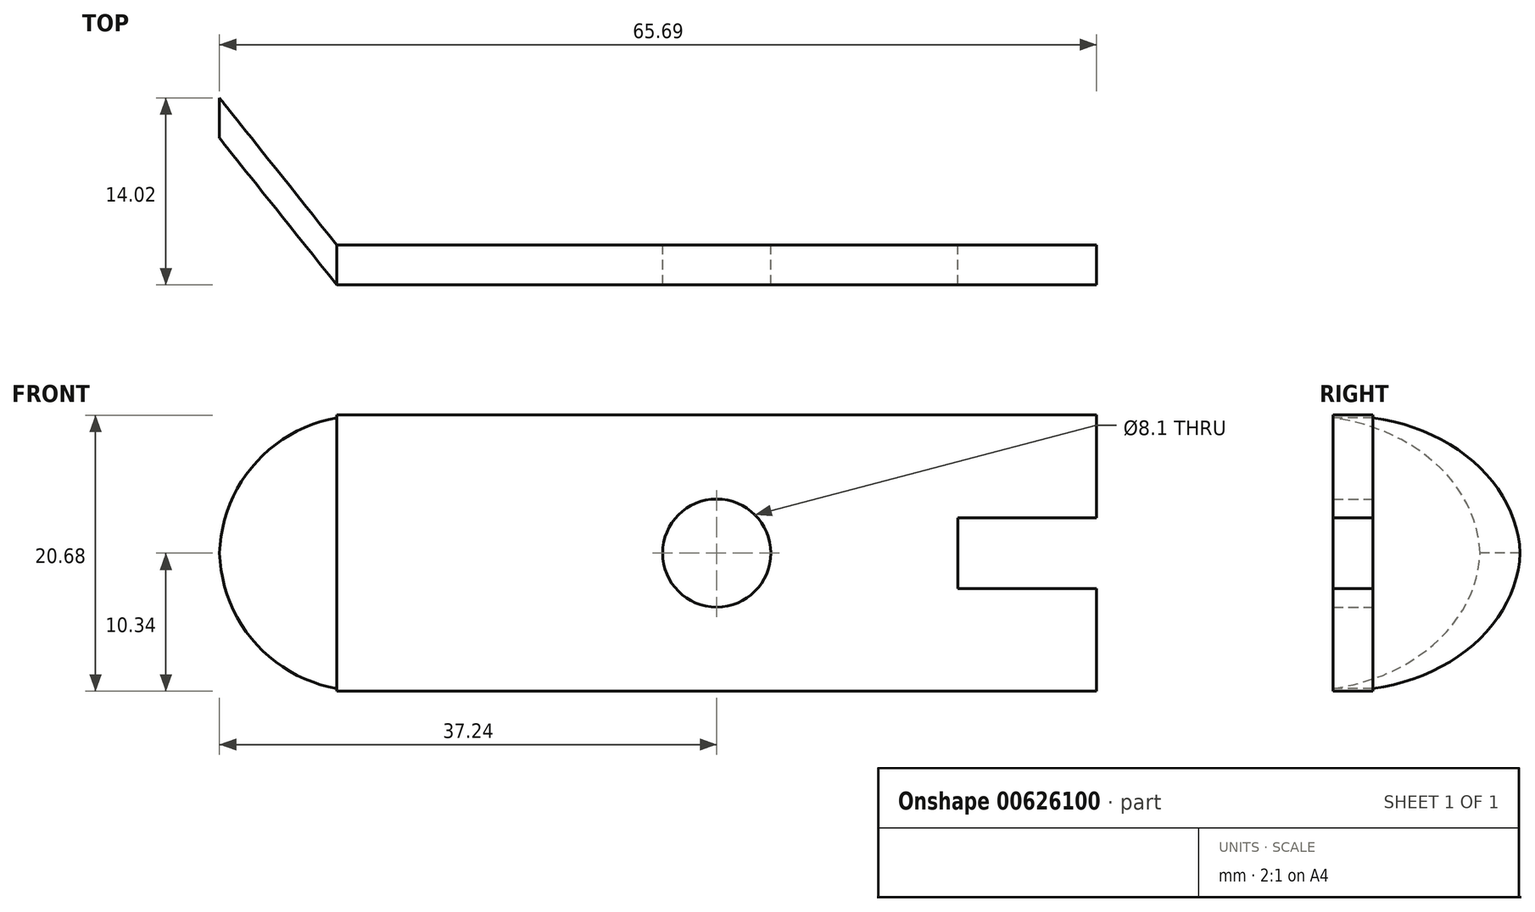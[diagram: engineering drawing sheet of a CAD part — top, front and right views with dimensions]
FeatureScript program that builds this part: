
annotation { "Feature Type Name" : "Feature", "Feature Type Description" : "" }
export const myFeature = defineFeature(function(context is Context, id is Id, definition is map)
    precondition{}
    {
        {
            var Q0;
            Q0=qCreatedBy(makeId("Front.planeOp"),FACE);
            var sketch = newSketch(context, id + "F0", { "sketchPlane" : qUnion([Q0])});
            skLineSegment(sketch, "E0.bottom", {"start": v(28.45, -10.34) * mm, "end": v(-28.45, -10.34) * mm});
            skLineSegment(sketch, "E0.top", {"start": v(28.45, 10.34) * mm, "end": v(-28.45, 10.34) * mm});
            skLineSegment(sketch, "E0.left", {"start": v(28.45, -10.34) * mm, "end": v(28.45, 10.34) * mm});
            skLineSegment(sketch, "E0.right", {"start": v(-28.45, -10.34) * mm, "end": v(-28.45, 10.34) * mm});
            skPoint(sketch, "E0.middle", {"position": v(0, 0) * mm});
            skLineSegment(sketch, "E1.bottom", {"start": v(38.85, -2.66) * mm, "end": v(18.05, -2.66) * mm});
            skLineSegment(sketch, "E1.top", {"start": v(38.85, 2.66) * mm, "end": v(18.05, 2.66) * mm});
            skLineSegment(sketch, "E1.left", {"start": v(38.85, -2.66) * mm, "end": v(38.85, 2.66) * mm});
            skLineSegment(sketch, "E1.right", {"start": v(18.05, -2.66) * mm, "end": v(18.05, 2.66) * mm});
            skPoint(sketch, "E1.middle", {"position": v(28.45, 0) * mm});
            skCircle(sketch, "E2", {"center": v(0, 0) * mm, "radius": 4.05 * mm});
            skSolve(sketch);
        }
        {
            var Q0;
            {var subQ4=sQuery(id+"F0.wireOp",EDGE,"E0.bottom");Q0=makeQuery(id+"F0.imprint","IMPRINT",FACE,{"disambiguationData":[TD([[makeQuery(id+"F0.imprint","IMPRINT",EDGE,{"derivedFrom":subQ4}),-1.0]])]});}
            extrude(context, id + "F1", {"entities" : qUnion([Q0]), "depth" : 3 * mm, "offsetDistance" : 25 * mm});
        }
        {
            var Q0;
            Q0=qCreatedBy(makeId("Top.planeOp"),FACE);
            var sketch = newSketch(context, id + "F2", { "sketchPlane" : qUnion([Q0])});
            skLineSegment(sketch, "E3", {"start": v(-28.45, 0) * mm, "end": v(-37.24, 11.02) * mm});
            skLineSegment(sketch, "E4", {"start": v(-37.24, 11.02) * mm, "end": v(-37.24, 8.02) * mm});
            skLineSegment(sketch, "E5", {"start": v(-37.24, 8.02) * mm, "end": v(-28.45, -3) * mm});
            skLineSegment(sketch, "E6", {"start": v(-28.45, 0) * mm, "end": v(-28.45, -3) * mm});
            skSolve(sketch);
        }
        {
            var Q0;
            Q0=makeQuery(id+"F2.imprint","IMPRINT",FACE,{"disambiguationData":[TD([[makeQuery(id+"F2.imprint","IMPRINT",EDGE,{"derivedFrom":sQuery(id+"F2.wireOp",EDGE,"E3")}),1.0]])]});
            extrude(context, id + "F3", {"entities" : qUnion([Q0]), "operationType" : NewBodyOperationType.ADD, "depth" : 20.3 * mm, "offsetDistance" : 25 * mm, "symmetric" : true});
        }
        {
            var Q0;
            Q0=makeQuery(id+"F3.opExtrude","CAP_EDGE",EDGE,{"disambiguationData":[OSD([sQuery(id+"F2.wireOp",EDGE,"E4")])],"isStart":false});
            var Q1;
            Q1=makeQuery(id+"F3.opExtrude","CAP_EDGE",EDGE,{"disambiguationData":[OSD([sQuery(id+"F2.wireOp",EDGE,"E4")])],"isStart":true});
            fillet(context, id + "F4", {"entities" : qUnion([Q0, Q1]), "radius" : 10.62 * mm, "tangentPropagation" : true, "allowEdgeOverflow" : false});
        }
    });
